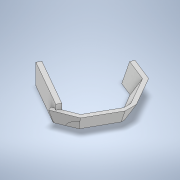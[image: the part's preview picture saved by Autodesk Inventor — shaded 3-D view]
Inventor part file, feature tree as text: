
AUTODESK INVENTOR PART (.ipt)
format: ipt  version: 2022 (Build 260153000, 153)  size: 189,952 bytes
history: native  units: in
note: dims shown in document units (in); Inventor stores cm internally (conversion verified against a paired STEP export)
features: sketch x4, plane x3, loft x1, extrude x1, split x1
ambient origin geometry x8: Origin, YZ Plane, XZ Plane, XY Plane, X Axis, Y Axis, Z Axis, Center Point
bodies: Solid1 (feature_tree)
feature tree (10):
  sketch  "Sketch1"  dims[d0=0.2441in d1=60.0deg]
  plane  "Work Plane2"
  loft  "Loft1"
  extrude  "Extrusion3"  Depth=0.202in
  sketch  "Sketch4"  dims[d7=0.0315in d8=0.0315in d11=0.1181in d14=0.0315in d15=0.0315in d16=0.0in d17=90.0deg d18=0.0in d19=90.0deg d20=0.1181in d27=0.0394in d28=0.1181in d29=0.0in d30=0.0in d31=-0.0276in]
  plane  "Work Plane3"
  split  "Split3"
  plane  "Work Plane1"
  sketch  "Sketch2"  dims[d2=0.1063in d3=0.202in]
  sketch  "Sketch3"  dims[d4=0.1181in]
